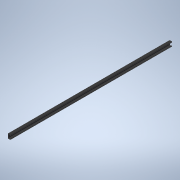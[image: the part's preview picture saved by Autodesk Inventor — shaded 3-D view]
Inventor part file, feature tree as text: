
AUTODESK INVENTOR PART (.ipt)
format: ipt  version: 2020 (Build 240168000, 168)  size: 112,128 bytes
history: native  units: mm
features: extrude x1, sketch x1
ambient origin geometry x8: Origin, YZ Plane, XZ Plane, XY Plane, X Axis, Y Axis, Z Axis, Center Point
bodies: Solid1 (feature_tree)
feature tree (2):
  extrude  "Extrusion1"  Depth=150.0mm
  sketch  "Sketch1"  dims[d0=80.0mm d1=150.0mm d2=25.0mm d3=25.0mm d4=3.5mm d5=5740.0mm d6=0.0mm]
